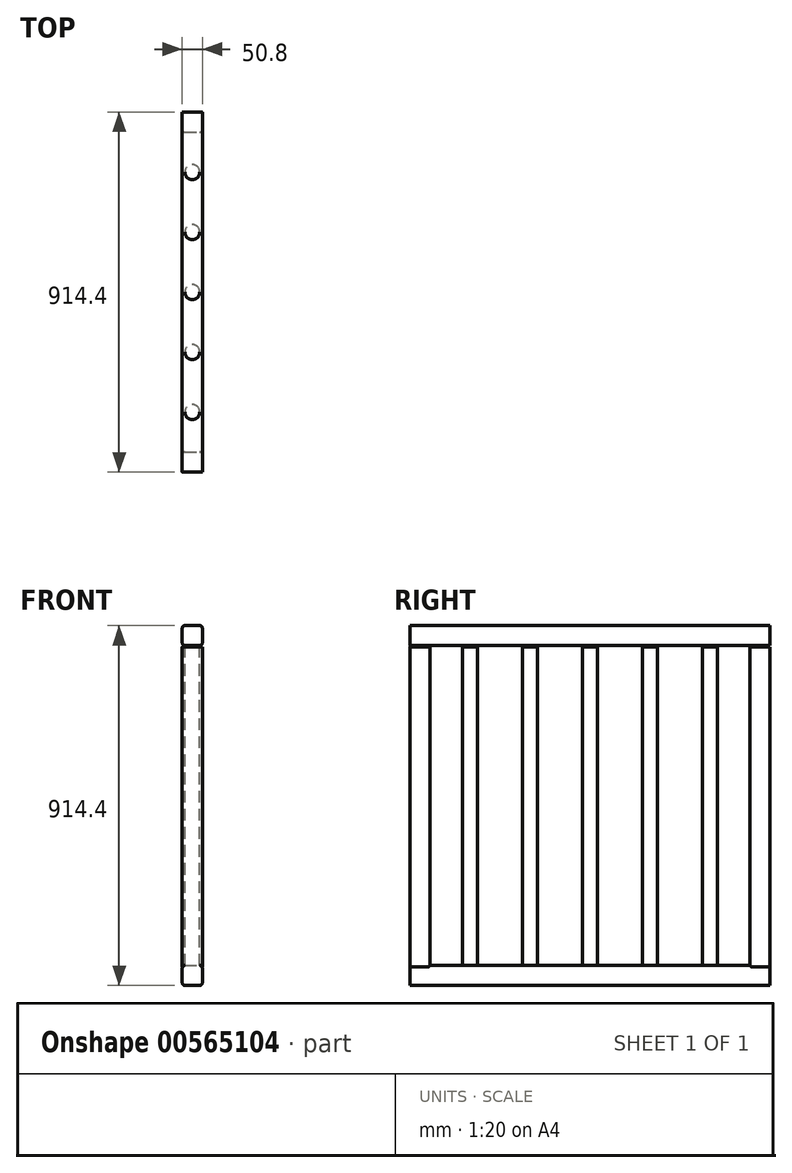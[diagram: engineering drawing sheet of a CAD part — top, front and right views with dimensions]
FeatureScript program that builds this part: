
annotation { "Feature Type Name" : "Feature", "Feature Type Description" : "" }
export const myFeature = defineFeature(function(context is Context, id is Id, definition is map)
    precondition{}
    {
        {
            var Q0;
            Q0=qCreatedBy(makeId("Front.planeOp"),FACE);
            var sketch = newSketch(context, id + "F0", { "sketchPlane" : qUnion([Q0])});
            skLineSegment(sketch, "E0.bottom", {"start": v(19.05, 84.05) * mm, "end": v(-19.05, 84.05) * mm});
            skLineSegment(sketch, "E0.top", {"start": v(19.05, 134.85) * mm, "end": v(-19.05, 134.85) * mm});
            skLineSegment(sketch, "E0.left", {"start": v(25.4, 90.4) * mm, "end": v(25.4, 128.5) * mm});
            skLineSegment(sketch, "E0.right", {"start": v(-25.4, 90.4) * mm, "end": v(-25.4, 128.5) * mm});
            skPoint(sketch, "E0.middle", {"position": v(0, 109.45) * mm});
            skLineSegment(sketch, "E1.bottom", {"start": v(19.05, -728.75) * mm, "end": v(-19.05, -728.75) * mm});
            skLineSegment(sketch, "E1.top", {"start": v(19.05, -779.55) * mm, "end": v(-19.05, -779.55) * mm});
            skLineSegment(sketch, "E1.left", {"start": v(25.4, -735.1) * mm, "end": v(25.4, -773.2) * mm});
            skLineSegment(sketch, "E1.right", {"start": v(-25.4, -735.1) * mm, "end": v(-25.4, -773.2) * mm});
            skPoint(sketch, "E1.middle", {"position": v(0, -754.15) * mm});
            skPoint(sketch, "E2.visualSharp", {"position": v(-25.4, 134.85) * mm});
            skArc(sketch, "E2.filletArc", {"start": v(-19.05, 134.85) * mm, "mid": v(-23.54, 133) * mm, "end": v(-25.4, 128.5) * mm});
            skPoint(sketch, "E3.visualSharp", {"position": v(25.4, 134.85) * mm});
            skArc(sketch, "E3.filletArc", {"start": v(25.4, 128.5) * mm, "mid": v(23.54, 133) * mm, "end": v(19.05, 134.85) * mm});
            skPoint(sketch, "E4.visualSharp", {"position": v(25.4, 84.05) * mm});
            skArc(sketch, "E4.filletArc", {"start": v(19.05, 84.05) * mm, "mid": v(23.54, 85.91) * mm, "end": v(25.4, 90.4) * mm});
            skPoint(sketch, "E5.visualSharp", {"position": v(-25.4, 84.05) * mm});
            skArc(sketch, "E5.filletArc", {"start": v(-25.4, 90.4) * mm, "mid": v(-23.54, 85.91) * mm, "end": v(-19.05, 84.05) * mm});
            skPoint(sketch, "E6.visualSharp", {"position": v(-25.4, -728.75) * mm});
            skArc(sketch, "E6.filletArc", {"start": v(-19.05, -728.75) * mm, "mid": v(-23.54, -730.6) * mm, "end": v(-25.4, -735.1) * mm});
            skPoint(sketch, "E7.visualSharp", {"position": v(25.4, -728.75) * mm});
            skArc(sketch, "E7.filletArc", {"start": v(25.4, -735.1) * mm, "mid": v(23.54, -730.6) * mm, "end": v(19.05, -728.75) * mm});
            skPoint(sketch, "E8.visualSharp", {"position": v(25.4, -779.55) * mm});
            skArc(sketch, "E8.filletArc", {"start": v(19.05, -779.55) * mm, "mid": v(23.54, -777.69) * mm, "end": v(25.4, -773.2) * mm});
            skPoint(sketch, "E9.visualSharp", {"position": v(-25.4, -779.55) * mm});
            skArc(sketch, "E9.filletArc", {"start": v(-25.4, -773.2) * mm, "mid": v(-23.54, -777.69) * mm, "end": v(-19.05, -779.55) * mm});
            skSolve(sketch);
        }
        {
            var Q0;
            Q0=makeQuery(id+"F0.imprint","IMPRINT",FACE,{"disambiguationData":[TD([[makeQuery(id+"F0.imprint","IMPRINT",EDGE,{"derivedFrom":sQuery(id+"F0.wireOp",EDGE,"E0.bottom")}),-1.0]])]});
            var Q1;
            Q1=makeQuery(id+"F0.imprint","IMPRINT",FACE,{"disambiguationData":[TD([[makeQuery(id+"F0.imprint","IMPRINT",EDGE,{"derivedFrom":sQuery(id+"F0.wireOp",EDGE,"E1.bottom")}),1.0]])]});
            extrude(context, id + "F1", {"entities" : qUnion([Q0, Q1]), "depth" : 914.4 * mm, "offsetDistance" : 25.4 * mm});
        }
        {
            var Q0;
            Q0=qCreatedBy(makeId("Top.planeOp"),FACE);
            cPlane(context, id + "F2", {"entities" : qUnion([Q0]), "cplaneType" : CPlaneType.OFFSET, "offset" : 81 * mm, "width" : 152.4 * mm, "height" : 152.4 * mm});
        }
        {
            var Q0;
            Q0=qCreatedBy(id+"F2.planeOp",FACE);
            var sketch = newSketch(context, id + "F3", { "sketchPlane" : qUnion([Q0])});
            skCircle(sketch, "E10", {"center": v(0, -152.4) * mm, "radius": 19.05 * mm});
            skCircle(sketch, "E11", {"center": v(0, -304.8) * mm, "radius": 19.05 * mm});
            skCircle(sketch, "E12", {"center": v(0, -609.6) * mm, "radius": 19.05 * mm});
            skCircle(sketch, "E13", {"center": v(0, -762) * mm, "radius": 19.05 * mm});
            skCircle(sketch, "E14", {"center": v(0, -457.2) * mm, "radius": 19.05 * mm});
            skLineSegment(sketch, "E15.bottom", {"start": v(19.05, 0) * mm, "end": v(-19.05, 0) * mm});
            skLineSegment(sketch, "E15.top", {"start": v(19.05, -50.8) * mm, "end": v(-19.05, -50.8) * mm});
            skLineSegment(sketch, "E15.left", {"start": v(25.4, -6.35) * mm, "end": v(25.4, -44.45) * mm});
            skLineSegment(sketch, "E15.right", {"start": v(-25.4, -6.35) * mm, "end": v(-25.4, -44.45) * mm});
            skPoint(sketch, "E15.middle", {"position": v(0, -25.4) * mm});
            skLineSegment(sketch, "E16.bottom", {"start": v(19.05, -863.6) * mm, "end": v(-19.05, -863.6) * mm});
            skLineSegment(sketch, "E16.top", {"start": v(19.05, -914.4) * mm, "end": v(-19.05, -914.4) * mm});
            skLineSegment(sketch, "E16.left", {"start": v(25.4, -869.95) * mm, "end": v(25.4, -908.05) * mm});
            skLineSegment(sketch, "E16.right", {"start": v(-25.4, -869.95) * mm, "end": v(-25.4, -908.05) * mm});
            skPoint(sketch, "E16.middle", {"position": v(0, -889) * mm});
            skPoint(sketch, "E17.visualSharp", {"position": v(25.4, 0) * mm});
            skArc(sketch, "E17.filletArc", {"start": v(25.4, -6.35) * mm, "mid": v(23.54, -1.86) * mm, "end": v(19.05, 0) * mm});
            skPoint(sketch, "E18.visualSharp", {"position": v(-25.4, 0) * mm});
            skArc(sketch, "E18.filletArc", {"start": v(-19.05, 0) * mm, "mid": v(-23.54, -1.86) * mm, "end": v(-25.4, -6.35) * mm});
            skPoint(sketch, "E19.visualSharp", {"position": v(-25.4, -50.8) * mm});
            skArc(sketch, "E19.filletArc", {"start": v(-25.4, -44.45) * mm, "mid": v(-23.54, -48.94) * mm, "end": v(-19.05, -50.8) * mm});
            skPoint(sketch, "E20.visualSharp", {"position": v(25.4, -50.8) * mm});
            skArc(sketch, "E20.filletArc", {"start": v(19.05, -50.8) * mm, "mid": v(23.54, -48.94) * mm, "end": v(25.4, -44.45) * mm});
            skPoint(sketch, "E21.visualSharp", {"position": v(25.4, -863.6) * mm});
            skArc(sketch, "E21.filletArc", {"start": v(25.4, -869.95) * mm, "mid": v(23.54, -865.46) * mm, "end": v(19.05, -863.6) * mm});
            skPoint(sketch, "E22.visualSharp", {"position": v(-25.4, -863.6) * mm});
            skArc(sketch, "E22.filletArc", {"start": v(-19.05, -863.6) * mm, "mid": v(-23.54, -865.46) * mm, "end": v(-25.4, -869.95) * mm});
            skPoint(sketch, "E23.visualSharp", {"position": v(-25.4, -914.4) * mm});
            skArc(sketch, "E23.filletArc", {"start": v(-25.4, -908.05) * mm, "mid": v(-23.54, -912.54) * mm, "end": v(-19.05, -914.4) * mm});
            skPoint(sketch, "E24.visualSharp", {"position": v(25.4, -914.4) * mm});
            skArc(sketch, "E24.filletArc", {"start": v(19.05, -914.4) * mm, "mid": v(23.54, -912.54) * mm, "end": v(25.4, -908.05) * mm});
            skSolve(sketch);
        }
        {
            var Q0;
            Q0 = qSketchRegion(id + "F3", true);
            extrude(context, id + "F4", {"entities" : qUnion([Q0]), "operationType" : NewBodyOperationType.ADD, "oppositeDirection" : true, "depth" : 812.8 * mm, "offsetDistance" : 25.4 * mm});
        }
    });
